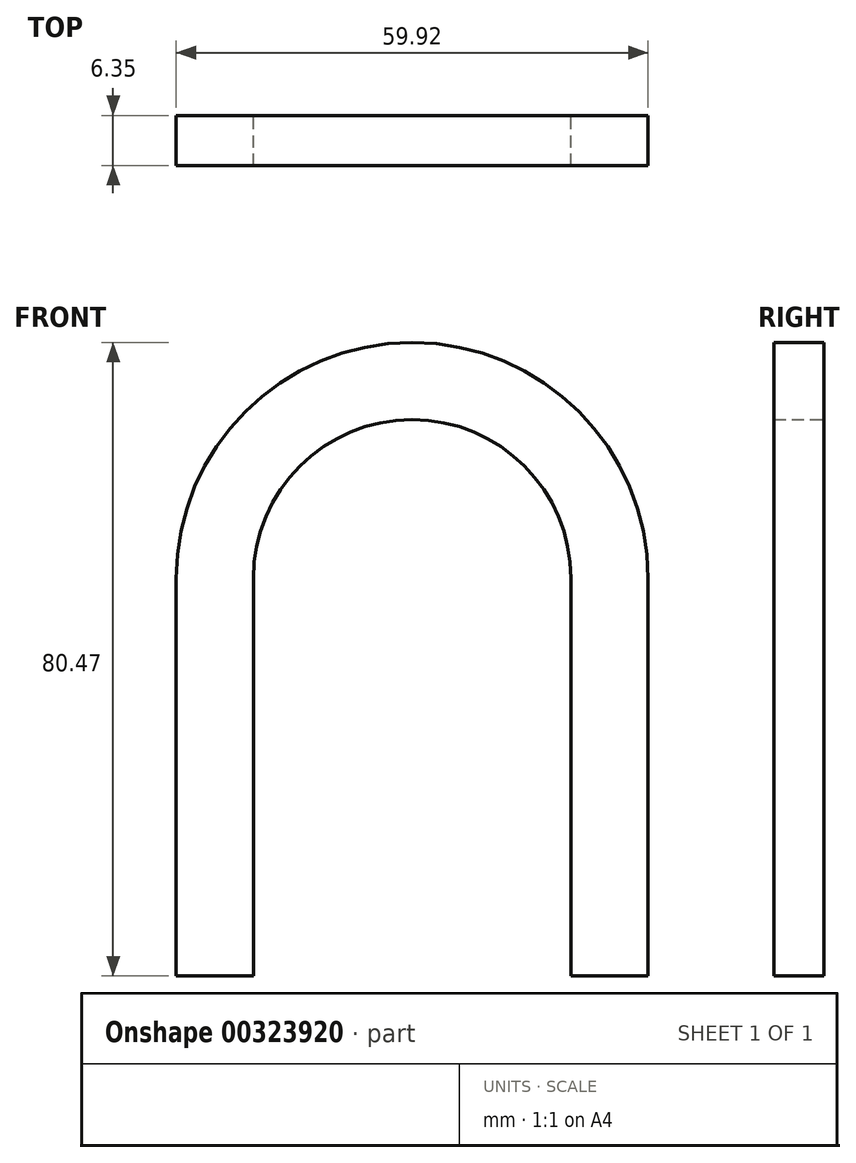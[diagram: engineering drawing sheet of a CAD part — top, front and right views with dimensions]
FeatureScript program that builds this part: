
annotation { "Feature Type Name" : "Feature", "Feature Type Description" : "" }
export const myFeature = defineFeature(function(context is Context, id is Id, definition is map)
    precondition{}
    {
        {
            var Q0;
            Q0=qCreatedBy(makeId("Front.planeOp"),FACE);
            var sketch = newSketch(context, id + "F0", { "sketchPlane" : qUnion([Q0])});
            skLineSegment(sketch, "E0", {"start": v(-38.57, -31.52) * mm, "end": v(-38.57, 19) * mm});
            skLineSegment(sketch, "E1", {"start": v(21.35, -31.52) * mm, "end": v(21.35, 19) * mm});
            skArc(sketch, "E2", {"start": v(21.35, 19) * mm, "mid": v(-8.6, 48.95) * mm, "end": v(-38.57, 19) * mm});
            skLineSegment(sketch, "E3", {"start": v(-38.57, -31.52) * mm, "end": v(-28.78, -31.52) * mm});
            skLineSegment(sketch, "E4", {"start": v(-28.78, -31.52) * mm, "end": v(-28.78, 19) * mm});
            skLineSegment(sketch, "E5", {"start": v(21.35, -31.52) * mm, "end": v(11.56, -31.52) * mm});
            skLineSegment(sketch, "E6", {"start": v(11.56, -31.52) * mm, "end": v(11.56, 19) * mm});
            skArc(sketch, "E7", {"start": v(11.56, 19) * mm, "mid": v(-8.6, 39.16) * mm, "end": v(-28.78, 19) * mm});
            skSolve(sketch);
        }
        {
            var Q0;
            Q0=makeQuery(id+"F0.imprint","IMPRINT",FACE,{"disambiguationData":[TD([[makeQuery(id+"F0.imprint","IMPRINT",EDGE,{"derivedFrom":sQuery(id+"F0.wireOp",EDGE,"E0")}),-1.0]])]});
            extrude(context, id + "F1", {"entities" : qUnion([Q0]), "depth" : 6.35 * mm});
        }
    });
